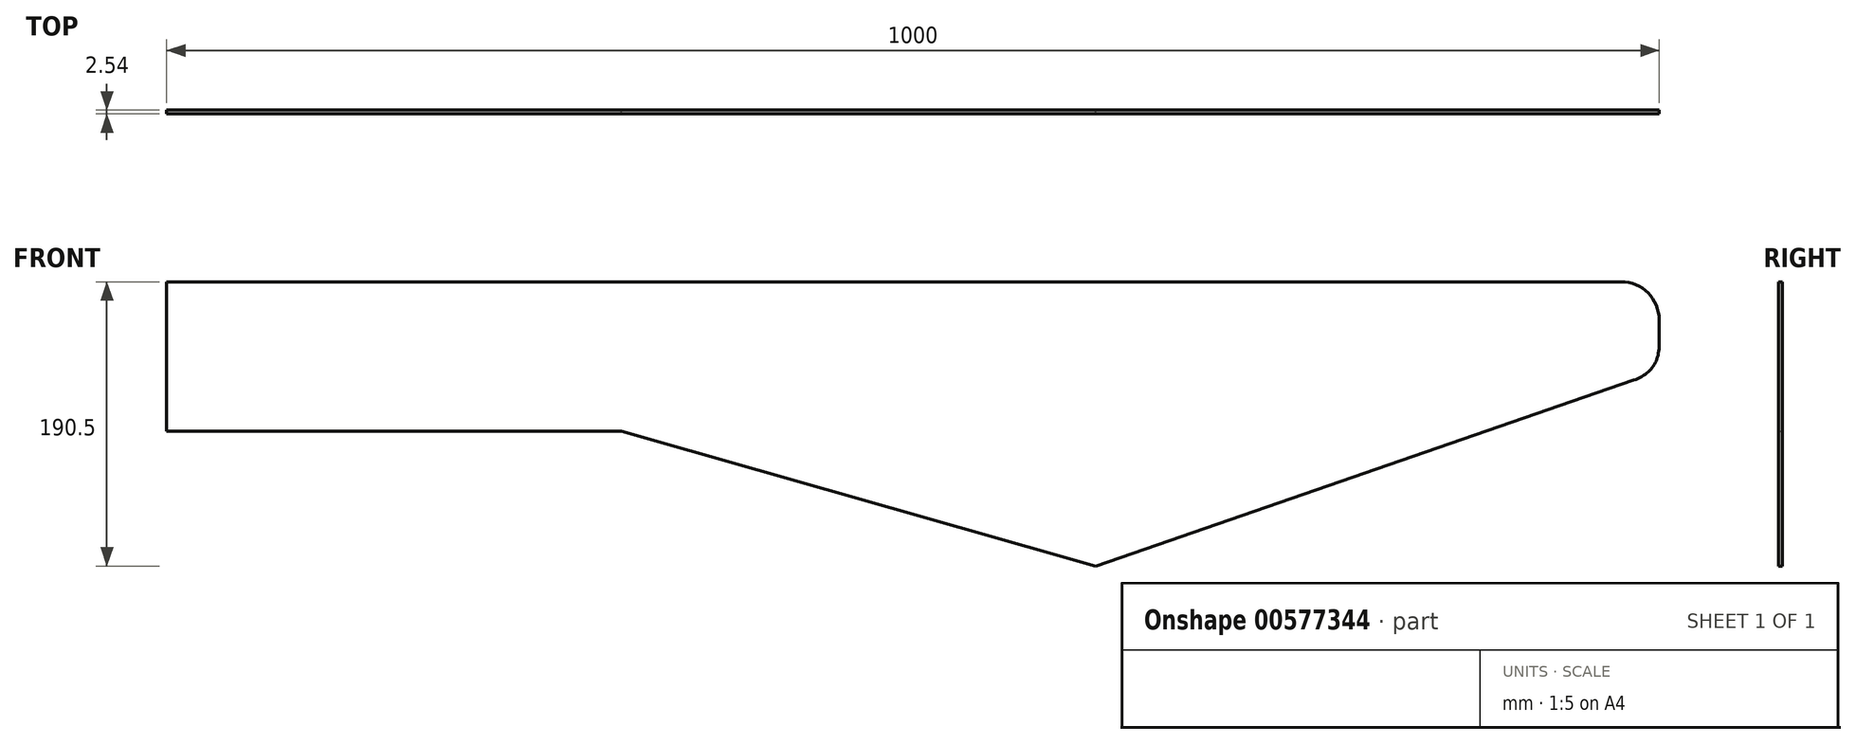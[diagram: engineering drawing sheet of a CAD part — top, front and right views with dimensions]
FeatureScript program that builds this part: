
annotation { "Feature Type Name" : "Feature", "Feature Type Description" : "" }
export const myFeature = defineFeature(function(context is Context, id is Id, definition is map)
    precondition{}
    {
        {
            var Q0;
            Q0=qCreatedBy(makeId("Front.planeOp"),FACE);
            var sketch = newSketch(context, id + "F0", { "sketchPlane" : qUnion([Q0])});
            skLineSegment(sketch, "E0", {"start": v(-366.43, 64.48) * mm, "end": v(633.57, 64.48) * mm});
            skLineSegment(sketch, "E1", {"start": v(633.57, 64.48) * mm, "end": v(633.57, 4.48) * mm});
            skLineSegment(sketch, "E2", {"start": v(633.57, 4.48) * mm, "end": v(255.92, -126.02) * mm});
            skLineSegment(sketch, "E3", {"start": v(255.92, -126.02) * mm, "end": v(-61.63, -35.52) * mm});
            skLineSegment(sketch, "E4", {"start": v(-61.63, -35.52) * mm, "end": v(-366.43, -35.52) * mm});
            skLineSegment(sketch, "E5", {"start": v(-366.43, -35.52) * mm, "end": v(-366.43, 64.48) * mm});
            skSolve(sketch);
        }
        {
            var Q0;
            Q0=makeQuery(id+"F0.imprint","IMPRINT",FACE,{"disambiguationData":[TD([[makeQuery(id+"F0.imprint","IMPRINT",EDGE,{"derivedFrom":sQuery(id+"F0.wireOp",EDGE,"E0")}),-1.0]])]});
            extrude(context, id + "F1", {"entities" : qUnion([Q0]), "depth" : 2.54 * mm, "offsetDistance" : 25.4 * mm});
        }
        {
            var Q0;
            Q0=makeQuery(id+"F1.opExtrude","SWEPT_EDGE",EDGE,{"disambiguationData":[OSD([sQuery(id+"F0.wireOp",EDGE,"E0"),sQuery(id+"F0.wireOp",EDGE,"E1")])]});
            fillet(context, id + "F2", {"entities" : qUnion([Q0]), "radius" : 25.4 * mm, "tangentPropagation" : true, "allowEdgeOverflow" : false});
        }
        {
            var Q0;
            Q0=makeQuery(id+"F1.opExtrude","SWEPT_EDGE",EDGE,{"disambiguationData":[OSD([sQuery(id+"F0.wireOp",EDGE,"E1"),sQuery(id+"F0.wireOp",EDGE,"E2")])]});
            fillet(context, id + "F3", {"entities" : qUnion([Q0]), "radius" : 25.4 * mm, "tangentPropagation" : true, "rho" : 0.5, "crossSection" : FilletCrossSection.CONIC, "allowEdgeOverflow" : false});
        }
    });
